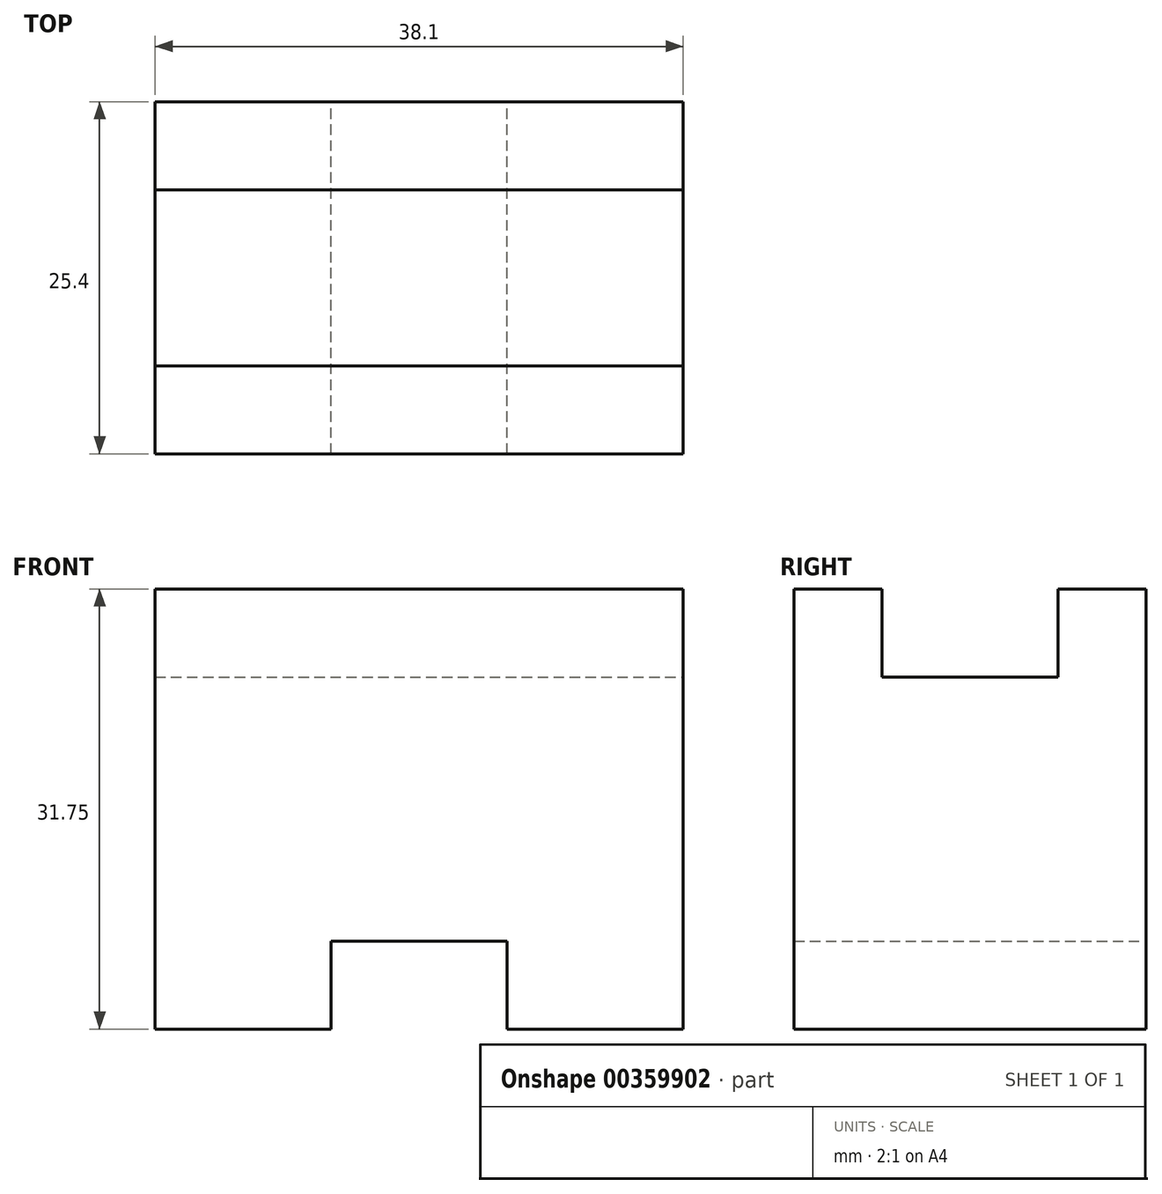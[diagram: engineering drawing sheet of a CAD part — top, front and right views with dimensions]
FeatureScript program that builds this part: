
annotation { "Feature Type Name" : "Feature", "Feature Type Description" : "" }
export const myFeature = defineFeature(function(context is Context, id is Id, definition is map)
    precondition{}
    {
        {
            var Q0;
            Q0=qCreatedBy(makeId("Front.planeOp"),FACE);
            var sketch = newSketch(context, id + "F0", { "sketchPlane" : qUnion([Q0])});
            skLineSegment(sketch, "E0", {"start": v(0, 0) * mm, "end": v(0, 31.75) * mm});
            skLineSegment(sketch, "E1", {"start": v(0, 31.75) * mm, "end": v(38.1, 31.75) * mm});
            skLineSegment(sketch, "E2", {"start": v(38.1, 31.75) * mm, "end": v(38.1, 0) * mm});
            skLineSegment(sketch, "E3", {"start": v(38.1, 0) * mm, "end": v(25.4, 0) * mm});
            skLineSegment(sketch, "E4", {"start": v(25.4, 0) * mm, "end": v(25.4, 6.35) * mm});
            skLineSegment(sketch, "E5", {"start": v(25.4, 6.35) * mm, "end": v(12.7, 6.35) * mm});
            skLineSegment(sketch, "E6", {"start": v(12.7, 6.35) * mm, "end": v(12.7, 0) * mm});
            skLineSegment(sketch, "E7", {"start": v(12.7, 0) * mm, "end": v(0, 0) * mm});
            skSolve(sketch);
        }
        {
            var Q0;
            Q0 = qSketchRegion(id + "F0", true);
            var Q1;
            Q1=makeQuery(id+"F0.imprint","IMPRINT",FACE,{"disambiguationData":[TD([[makeQuery(id+"F0.imprint","IMPRINT",EDGE,{"derivedFrom":sQuery(id+"F0.wireOp",EDGE,"E0")}),-1.0]])]});
            extrude(context, id + "F1", {"entities" : qUnion([Q0, Q1]), "depth" : 25.4 * mm});
        }
        {
            var Q0;
            Q0=makeQuery(id+"F1.opExtrude","SWEPT_FACE",FACE,{"disambiguationData":[OSD([sQuery(id+"F0.wireOp",EDGE,"E1")])]});
            var sketch = newSketch(context, id + "F2", { "sketchPlane" : qUnion([Q0])});
            skLineSegment(sketch, "E8", {"start": v(0, -6.35) * mm, "end": v(38.1, -6.35) * mm});
            skLineSegment(sketch, "E9", {"start": v(38.1, -6.35) * mm, "end": v(38.1, -19.05) * mm});
            skLineSegment(sketch, "E10", {"start": v(38.1, -19.05) * mm, "end": v(0, -19.05) * mm});
            skLineSegment(sketch, "E11", {"start": v(0, -19.05) * mm, "end": v(0, -6.35) * mm});
            skLineSegment(sketch, "E12", {"start": v(0, 0) * mm, "end": v(0, -25.4) * mm});
            skLineSegment(sketch, "E13", {"start": v(0, -25.4) * mm, "end": v(38.1, -25.4) * mm});
            skLineSegment(sketch, "E14", {"start": v(38.1, -25.4) * mm, "end": v(38.1, 0) * mm});
            skLineSegment(sketch, "E15", {"start": v(38.1, 0) * mm, "end": v(0, 0) * mm});
            skSolve(sketch);
        }
        {
            var Q0;
            {var subQ0=sQuery(id+"F2.wireOp",EDGE,"E8");Q0=makeQuery(id+"F2.imprint","IMPRINT",FACE,{"disambiguationData":[TD([[makeQuery(id+"F2.imprint","IMPRINT",EDGE,{"derivedFrom":subQ0}),-1.0]])]});}
            extrude(context, id + "F3", {"entities" : qUnion([Q0]), "operationType" : NewBodyOperationType.REMOVE, "oppositeDirection" : true, "depth" : 6.35 * mm});
        }
    });
